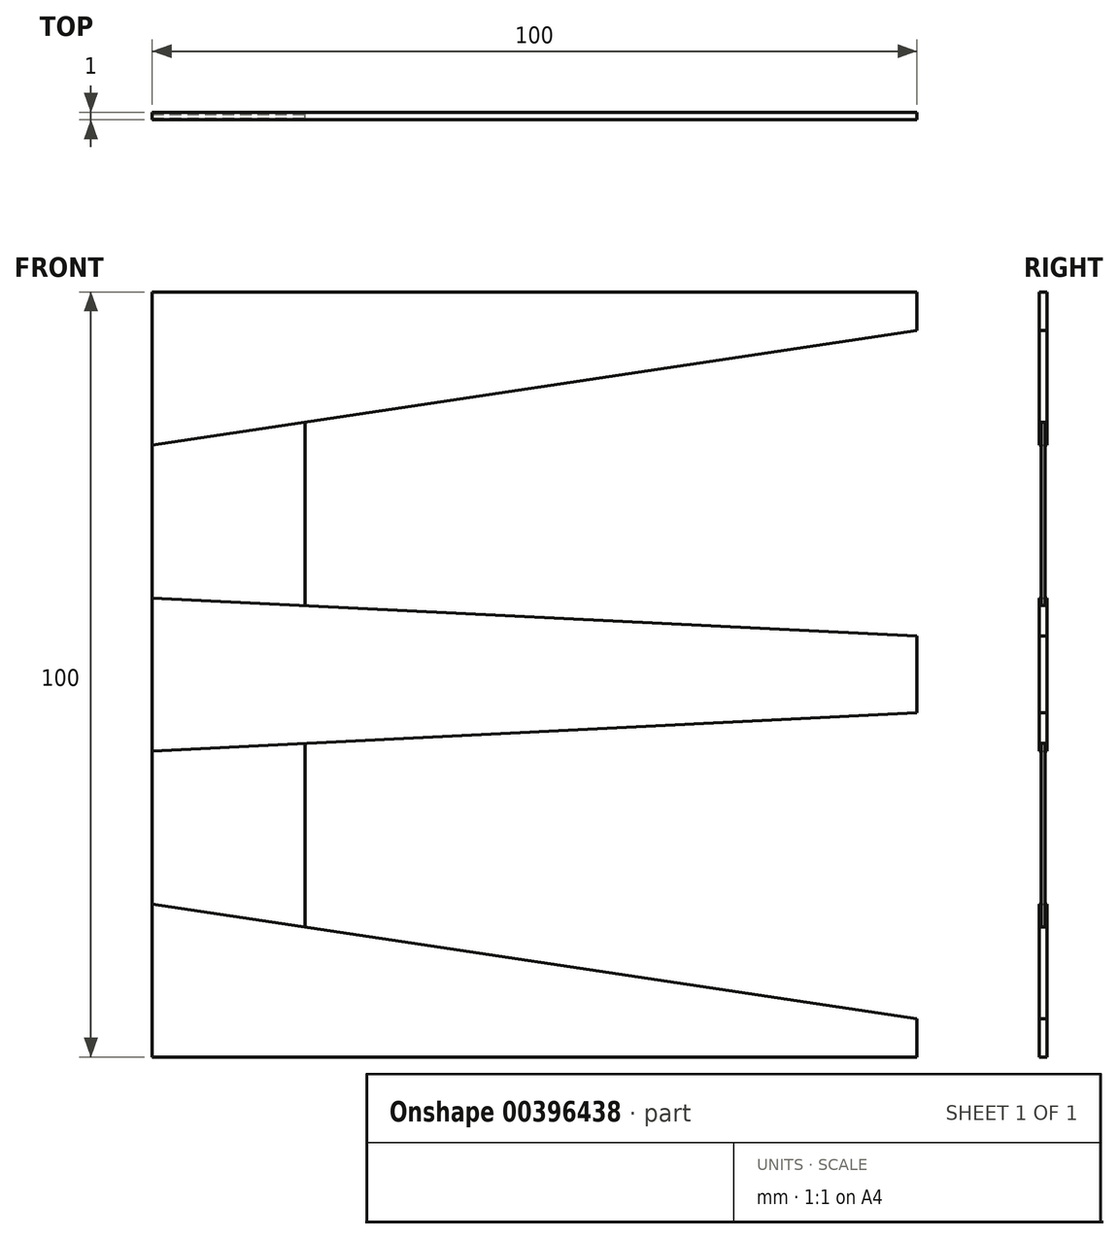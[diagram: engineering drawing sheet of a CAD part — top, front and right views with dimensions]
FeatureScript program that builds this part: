
annotation { "Feature Type Name" : "Feature", "Feature Type Description" : "" }
export const myFeature = defineFeature(function(context is Context, id is Id, definition is map)
    precondition{}
    {
        {
            var Q0;
            Q0=qCreatedBy(makeId("Front.planeOp"),FACE);
            var sketch = newSketch(context, id + "F0", { "sketchPlane" : qUnion([Q0])});
            skLineSegment(sketch, "E0.bottom", {"start": v(50, -50) * mm, "end": v(-50, -50) * mm});
            skLineSegment(sketch, "E0.top", {"start": v(50, 50) * mm, "end": v(-50, 50) * mm});
            skLineSegment(sketch, "E0.left", {"start": v(50, -50) * mm, "end": v(50, 50) * mm});
            skLineSegment(sketch, "E0.right", {"start": v(-50, -50) * mm, "end": v(-50, 50) * mm});
            skPoint(sketch, "E0.middle", {"position": v(0, 0) * mm});
            skLineSegment(sketch, "E1", {"start": v(-50, 30) * mm, "end": v(50, 45) * mm});
            skLineSegment(sketch, "E2", {"start": v(-50, 10) * mm, "end": v(50, 5) * mm});
            skLineSegment(sketch, "E3", {"start": v(-50, -10) * mm, "end": v(50, -5) * mm});
            skLineSegment(sketch, "E4", {"start": v(-50, -30) * mm, "end": v(50, -45) * mm});
            skLineSegment(sketch, "E5", {"start": v(-30, 33) * mm, "end": v(-30, 9) * mm});
            skLineSegment(sketch, "E6", {"start": v(-30, -9) * mm, "end": v(-30, -33) * mm});
            skSolve(sketch);
        }
        {
            var Q0;
            {var subQ0=sQuery(id+"F0.wireOp",EDGE,"E0.top");Q0=makeQuery(id+"F0.imprint","IMPRINT",FACE,{"disambiguationData":[TD([[makeQuery(id+"F0.imprint","IMPRINT",EDGE,{"derivedFrom":subQ0}),1.0]])]});}
            var Q1;
            {var subQ0=sQuery(id+"F0.wireOp",EDGE,"E2");Q1=makeQuery(id+"F0.imprint","IMPRINT",FACE,{"disambiguationData":[TD([[makeQuery(id+"F0.imprint","IMPRINT",EDGE,{"derivedFrom":subQ0}),-1.0]])]});}
            var Q2;
            {var subQ0=sQuery(id+"F0.wireOp",EDGE,"E0.bottom");Q2=makeQuery(id+"F0.imprint","IMPRINT",FACE,{"disambiguationData":[TD([[makeQuery(id+"F0.imprint","IMPRINT",EDGE,{"derivedFrom":subQ0}),-1.0]])]});}
            extrude(context, id + "F1", {"entities" : qUnion([Q0, Q1, Q2]), "endBound" : BoundingType.SYMMETRIC, "depth" : 1 * mm});
        }
        {
            var Q0;
            {var subQ5=sQuery(id+"F0.wireOp",EDGE,"E5");Q0=makeQuery(id+"F0.imprint","IMPRINT",FACE,{"disambiguationData":[TD([[makeQuery(id+"F0.imprint","IMPRINT",EDGE,{"derivedFrom":subQ5}),-1.0]])]});}
            var Q1;
            {var subQ5=sQuery(id+"F0.wireOp",EDGE,"E6");Q1=makeQuery(id+"F0.imprint","IMPRINT",FACE,{"disambiguationData":[TD([[makeQuery(id+"F0.imprint","IMPRINT",EDGE,{"derivedFrom":subQ5}),-1.0]])]});}
            extrude(context, id + "F2", {"entities" : qUnion([Q0, Q1]), "endBound" : BoundingType.SYMMETRIC, "depth" : 0.5 * mm});
        }
    });
